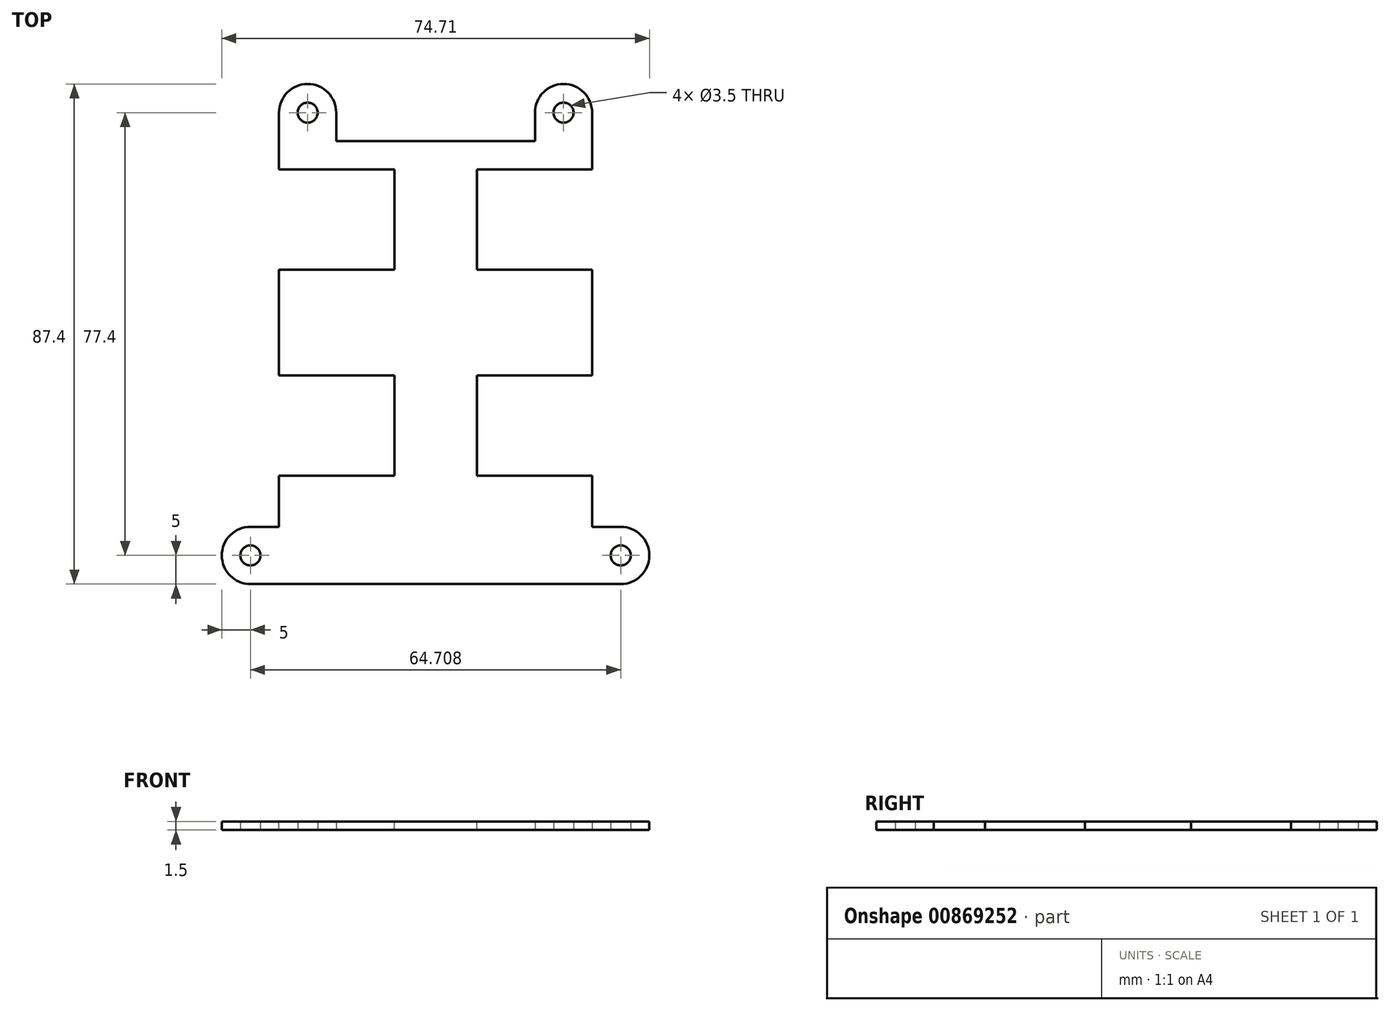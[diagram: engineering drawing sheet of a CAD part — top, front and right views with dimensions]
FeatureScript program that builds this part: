
annotation { "Feature Type Name" : "Feature", "Feature Type Description" : "" }
export const myFeature = defineFeature(function(context is Context, id is Id, definition is map)
    precondition{}
    {
        {
            var Q0;
            Q0=qCreatedBy(makeId("Top.planeOp"),FACE);
            var sketch = newSketch(context, id + "F0", { "sketchPlane" : qUnion([Q0])});
            skLineSegment(sketch, "E0.bottom", {"start": v(0, 0) * mm, "end": v(51.3, 0) * mm});
            skLineSegment(sketch, "E0.top", {"start": v(0, 74) * mm, "end": v(51.3, 74) * mm});
            skLineSegment(sketch, "E0.left", {"start": v(0, 0) * mm, "end": v(0, 74) * mm});
            skLineSegment(sketch, "E0.right", {"start": v(51.3, 0) * mm, "end": v(51.3, 74) * mm});
            skLineSegment(sketch, "E1.bottom", {"start": v(0, 69) * mm, "end": v(16.7, 69) * mm, "construction": true});
            skLineSegment(sketch, "E1.top", {"start": v(0, 55) * mm, "end": v(16.7, 55) * mm, "construction": true});
            skLineSegment(sketch, "E1.left", {"start": v(0, 69) * mm, "end": v(0, 55) * mm, "construction": true});
            skLineSegment(sketch, "E1.right", {"start": v(16.7, 69) * mm, "end": v(16.7, 55) * mm, "construction": true});
            skLineSegment(sketch, "E2.bottom", {"start": v(0, 33) * mm, "end": v(16.7, 33) * mm, "construction": true});
            skLineSegment(sketch, "E2.top", {"start": v(0, 19) * mm, "end": v(16.7, 19) * mm, "construction": true});
            skLineSegment(sketch, "E2.left", {"start": v(0, 33) * mm, "end": v(0, 19) * mm, "construction": true});
            skLineSegment(sketch, "E2.right", {"start": v(16.7, 33) * mm, "end": v(16.7, 19) * mm, "construction": true});
            skLineSegment(sketch, "E3.bottom", {"start": v(51.3, 69) * mm, "end": v(34.6, 69) * mm, "construction": true});
            skLineSegment(sketch, "E3.top", {"start": v(51.3, 55) * mm, "end": v(34.6, 55) * mm, "construction": true});
            skLineSegment(sketch, "E3.left", {"start": v(51.3, 69) * mm, "end": v(51.3, 55) * mm, "construction": true});
            skLineSegment(sketch, "E3.right", {"start": v(34.6, 69) * mm, "end": v(34.6, 55) * mm, "construction": true});
            skLineSegment(sketch, "E4.bottom", {"start": v(51.3, 33) * mm, "end": v(34.6, 33) * mm, "construction": true});
            skLineSegment(sketch, "E4.top", {"start": v(51.3, 19) * mm, "end": v(34.6, 19) * mm, "construction": true});
            skLineSegment(sketch, "E4.left", {"start": v(51.3, 33) * mm, "end": v(51.3, 19) * mm, "construction": true});
            skLineSegment(sketch, "E4.right", {"start": v(34.6, 33) * mm, "end": v(34.6, 19) * mm, "construction": true});
            skCircle(sketch, "E5", {"center": v(11.21, 3.92) * mm, "radius": 1.6 * mm});
            skCircle(sketch, "E6", {"center": v(32.51, 3.92) * mm, "radius": 1.6 * mm});
            skCircle(sketch, "E7", {"center": v(49.43, 3.92) * mm, "radius": 1.6 * mm});
            skCircle(sketch, "E8", {"center": v(49.43, 72.12) * mm, "radius": 1.6 * mm});
            skCircle(sketch, "E9", {"center": v(1.88, 72.12) * mm, "radius": 1.6 * mm});
            skLineSegment(sketch, "E10", {"start": v(1.88, 72.12) * mm, "end": v(49.43, 72.12) * mm, "construction": true});
            skSolve(sketch);
        }
        {
            var Q0;
            {var subQ10=sQuery(id+"F0.wireOp",EDGE,"E0.bottom");Q0=makeQuery(id+"F0.imprint","IMPRINT",FACE,{"disambiguationData":[TD([[makeQuery(id+"F0.imprint","IMPRINT",EDGE,{"derivedFrom":subQ10}),1.0]])]});}
            var sketch = newSketch(context, id + "F1", { "sketchPlane" : qUnion([Q0])});
            skLineSegment(sketch, "E11.0", {"start": v(-1.7, -1.7) * mm, "end": v(-1.7, 75.7) * mm});
            skLineSegment(sketch, "E11.1", {"start": v(-1.7, -1.7) * mm, "end": v(53, -1.7) * mm});
            skLineSegment(sketch, "E11.2", {"start": v(53, -1.7) * mm, "end": v(53, 75.7) * mm});
            skLineSegment(sketch, "E11.3", {"start": v(-1.7, 75.7) * mm, "end": v(53, 75.7) * mm});
            skSolve(sketch);
        }
        {
            var Q0;
            Q0=qSketchRegion(id+"F1",true);
            extrude(context, id + "F2", {"entities" : qUnion([Q0]), "depth" : 1.5 * mm, "offsetDistance" : 25 * mm});
        }
        {
            var Q0;
            Q0=makeQuery(id+"F2.opExtrude","CAP_FACE",FACE,{"disambiguationData":[OSD([sQuery(id+"F1.wireOp",EDGE,"E11.0"),sQuery(id+"F1.wireOp",EDGE,"E11.1"),sQuery(id+"F1.wireOp",EDGE,"E11.2"),sQuery(id+"F1.wireOp",EDGE,"E11.3")])],"isStart":true});
            var sketch = newSketch(context, id + "F3", { "sketchPlane" : qUnion([Q0])});
            skArc(sketch, "E12", {"start": v(-6.7, 1.7) * mm, "mid": v(-11.7, -3.3) * mm, "end": v(-6.7, -8.3) * mm});
            skArc(sketch, "E13", {"start": v(-1.7, -80.7) * mm, "mid": v(3.3, -85.7) * mm, "end": v(8.3, -80.7) * mm});
            skLineSegment(sketch, "E14", {"start": v(-1.7, 1.7) * mm, "end": v(-6.7, 1.7) * mm});
            skLineSegment(sketch, "E15", {"start": v(-6.7, -8.3) * mm, "end": v(-1.7, -8.3) * mm});
            skLineSegment(sketch, "E16", {"start": v(25.65, 1.7) * mm, "end": v(25.65, -75.7) * mm, "construction": true});
            skLineSegment(sketch, "E17", {"start": v(-1.7, 1.7) * mm, "end": v(-1.7, -8.3) * mm});
            skLineSegment(sketch, "E18", {"start": v(-1.7, -75.7) * mm, "end": v(-1.7, -80.7) * mm});
            skLineSegment(sketch, "E19", {"start": v(8.3, -80.7) * mm, "end": v(8.3, -75.7) * mm});
            skLineSegment(sketch, "E20", {"start": v(-1.7, -75.7) * mm, "end": v(8.3, -75.7) * mm});
            skLineSegment(sketch, "E21.MirrorCS", {"start": v(58, -8.3) * mm, "end": v(53, -8.3) * mm});
            skLineSegment(sketch, "E22.MirrorCS", {"start": v(43, -80.7) * mm, "end": v(43, -75.7) * mm});
            skLineSegment(sketch, "E23.MirrorCS", {"start": v(53, 1.7) * mm, "end": v(58, 1.7) * mm});
            skLineSegment(sketch, "E24.MirrorCS", {"start": v(53, -75.7) * mm, "end": v(53, -80.7) * mm});
            skLineSegment(sketch, "E25.MirrorCS", {"start": v(53, 1.7) * mm, "end": v(53, -8.3) * mm});
            skLineSegment(sketch, "E26.MirrorCS", {"start": v(53, -75.7) * mm, "end": v(43, -75.7) * mm});
            skArc(sketch, "E27.MirrorCS", {"start": v(53, -80.7) * mm, "mid": v(48, -85.7) * mm, "end": v(43, -80.7) * mm});
            skArc(sketch, "E28.MirrorCS", {"start": v(58, 1.7) * mm, "mid": v(63, -3.3) * mm, "end": v(58, -8.3) * mm});
            skCircle(sketch, "E29", {"center": v(-6.7, -3.3) * mm, "radius": 1.75 * mm});
            skCircle(sketch, "E30", {"center": v(58, -3.3) * mm, "radius": 1.75 * mm});
            skCircle(sketch, "E31", {"center": v(48, -80.7) * mm, "radius": 1.75 * mm});
            skCircle(sketch, "E32", {"center": v(3.3, -80.7) * mm, "radius": 1.75 * mm});
            skSolve(sketch);
        }
        {
            var Q0;
            Q0=qSketchRegion(id+"F3",true);
            var Q1;
            {var subQ0=sQuery(id+"F1.wireOp",EDGE,"E11.0");var subQ1=sQuery(id+"F1.wireOp",EDGE,"E11.2");var subQ2=sQuery(id+"F1.wireOp",EDGE,"E11.3");Q1=makeQuery(id+"FCauK0S3PUZOb4y_1.boolean.opBoolean","SPLIT",FACE,{"disambiguationData":[TD([makeQuery(id+"F2.opExtrude","SWEPT_FACE",FACE,{"disambiguationData":[OSD([subQ2])]})])],"derivedFrom":makeQuery(id+"F2.opExtrude","CAP_FACE",FACE,{"disambiguationData":[OSD([subQ0,sQuery(id+"F1.wireOp",EDGE,"E11.1"),subQ1,subQ2])],"isStart":false})});}
            extrude(context, id + "F4", {"entities" : qUnion([Q0]), "operationType" : NewBodyOperationType.ADD, "oppositeDirection" : true, "depth" : 1.5 * mm, "endBoundEntityFace" : qUnion([Q1]), "offsetDistance" : 25 * mm});
        }
        {
            var Q0;
            Q0=makeQuery(id+"F4.boolean.opBoolean","MERGE",FACE,{"derivedFrom":[makeQuery(id+"F2.opExtrude","CAP_FACE",FACE,{"disambiguationData":[OSD([sQuery(id+"F1.wireOp",EDGE,"E11.0"),sQuery(id+"F1.wireOp",EDGE,"E11.1"),sQuery(id+"F1.wireOp",EDGE,"E11.2"),sQuery(id+"F1.wireOp",EDGE,"E11.3")])],"isStart":false}),makeQuery(id+"F4.opExtrude","CAP_FACE",FACE,{"disambiguationData":[OSD([sQuery(id+"F3.wireOp",EDGE,"E12"),sQuery(id+"F3.wireOp",EDGE,"E14"),sQuery(id+"F3.wireOp",EDGE,"E15"),sQuery(id+"F3.wireOp",EDGE,"E17"),sQuery(id+"F3.wireOp",EDGE,"E29")])],"isStart":false}),makeQuery(id+"F4.opExtrude","CAP_FACE",FACE,{"disambiguationData":[OSD([sQuery(id+"F3.wireOp",EDGE,"E13"),sQuery(id+"F3.wireOp",EDGE,"E18"),sQuery(id+"F3.wireOp",EDGE,"E19"),sQuery(id+"F3.wireOp",EDGE,"E20"),sQuery(id+"F3.wireOp",EDGE,"E32")])],"isStart":false}),makeQuery(id+"F4.opExtrude","CAP_FACE",FACE,{"disambiguationData":[OSD([sQuery(id+"F3.wireOp",EDGE,"E21.MirrorCS"),sQuery(id+"F3.wireOp",EDGE,"E23.MirrorCS"),sQuery(id+"F3.wireOp",EDGE,"E25.MirrorCS"),sQuery(id+"F3.wireOp",EDGE,"E28.MirrorCS"),sQuery(id+"F3.wireOp",EDGE,"E30")])],"isStart":false}),makeQuery(id+"F4.opExtrude","CAP_FACE",FACE,{"disambiguationData":[OSD([sQuery(id+"F3.wireOp",EDGE,"E22.MirrorCS"),sQuery(id+"F3.wireOp",EDGE,"E24.MirrorCS"),sQuery(id+"F3.wireOp",EDGE,"E26.MirrorCS"),sQuery(id+"F3.wireOp",EDGE,"E27.MirrorCS"),sQuery(id+"F3.wireOp",EDGE,"E31")])],"isStart":false})]});
            var sketch = newSketch(context, id + "F5", { "sketchPlane" : qUnion([Q0])});
            skLineSegment(sketch, "E33.0", {"start": v(-1.75, 17.25) * mm, "end": v(18.45, 17.25) * mm});
            skLineSegment(sketch, "E33.1", {"start": v(-1.75, 34.75) * mm, "end": v(-1.75, 17.25) * mm});
            skLineSegment(sketch, "E33.2", {"start": v(-1.75, 34.75) * mm, "end": v(18.45, 34.75) * mm});
            skLineSegment(sketch, "E33.3", {"start": v(18.45, 34.75) * mm, "end": v(18.45, 17.25) * mm});
            skLineSegment(sketch, "E34.0", {"start": v(32.86, 34.75) * mm, "end": v(32.86, 17.25) * mm});
            skLineSegment(sketch, "E34.1", {"start": v(53.06, 34.75) * mm, "end": v(32.86, 34.75) * mm});
            skLineSegment(sketch, "E34.2", {"start": v(53.06, 34.75) * mm, "end": v(53.06, 17.25) * mm});
            skLineSegment(sketch, "E34.3", {"start": v(53.06, 17.25) * mm, "end": v(32.86, 17.25) * mm});
            skLineSegment(sketch, "E35.0", {"start": v(-1.75, 70.75) * mm, "end": v(18.45, 70.75) * mm});
            skLineSegment(sketch, "E35.1", {"start": v(-1.75, 70.75) * mm, "end": v(-1.75, 53.25) * mm});
            skLineSegment(sketch, "E35.2", {"start": v(-1.75, 53.25) * mm, "end": v(18.45, 53.25) * mm});
            skLineSegment(sketch, "E35.3", {"start": v(18.45, 70.75) * mm, "end": v(18.45, 53.25) * mm});
            skLineSegment(sketch, "E36.0", {"start": v(32.86, 70.75) * mm, "end": v(32.86, 53.25) * mm});
            skLineSegment(sketch, "E36.1", {"start": v(53.06, 70.75) * mm, "end": v(32.86, 70.75) * mm});
            skLineSegment(sketch, "E36.2", {"start": v(53.06, 70.75) * mm, "end": v(53.06, 53.25) * mm});
            skLineSegment(sketch, "E36.3", {"start": v(53.06, 53.25) * mm, "end": v(32.86, 53.25) * mm});
            skSolve(sketch);
        }
        {
            var Q0;
            Q0 = qSketchRegion(id + "F5", true);
            extrude(context, id + "F6", {"entities" : qUnion([Q0]), "operationType" : NewBodyOperationType.REMOVE, "endBound" : BoundingType.THROUGH_ALL, "oppositeDirection" : true, "depth" : 25 * mm, "offsetDistance" : 25 * mm});
        }
    });
